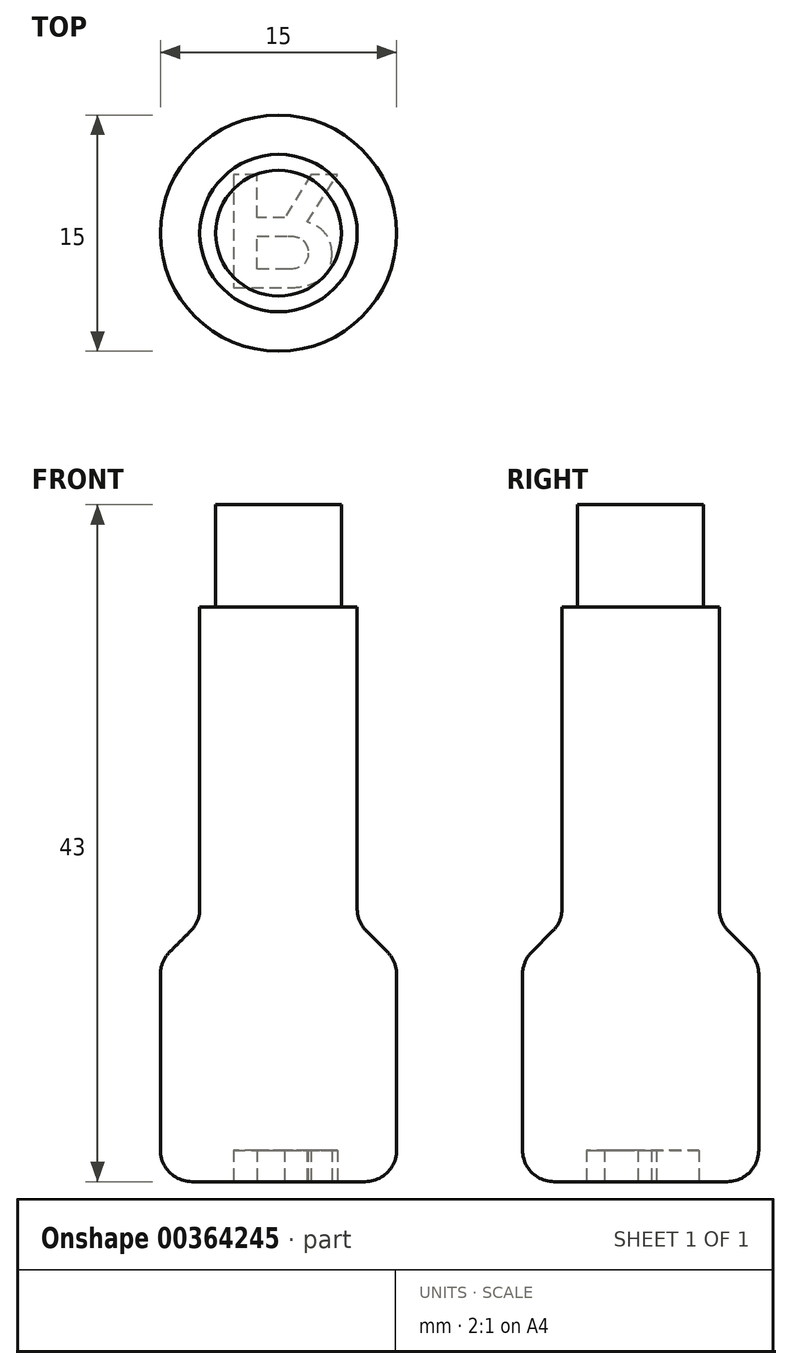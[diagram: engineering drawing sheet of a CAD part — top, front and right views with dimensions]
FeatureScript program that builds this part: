
annotation { "Feature Type Name" : "Feature", "Feature Type Description" : "" }
export const myFeature = defineFeature(function(context is Context, id is Id, definition is map)
    precondition{}
    {
        {
            var Q0;
            Q0=qCreatedBy(makeId("Right.planeOp"),FACE);
            var sketch = newSketch(context, id + "F0", { "sketchPlane" : qUnion([Q0])});
            skLineSegment(sketch, "E0", {"start": v(0, 0) * mm, "end": v(-7.5, 0) * mm});
            skLineSegment(sketch, "E1", {"start": v(-7.5, 0) * mm, "end": v(-7.5, 14) * mm});
            skLineSegment(sketch, "E2", {"start": v(-7.5, 14) * mm, "end": v(-5, 16.5) * mm});
            skLineSegment(sketch, "E3", {"start": v(-5, 16.5) * mm, "end": v(-5, 36.5) * mm});
            skLineSegment(sketch, "E4", {"start": v(-5, 36.5) * mm, "end": v(-4, 36.5) * mm});
            skLineSegment(sketch, "E5", {"start": v(-4, 36.5) * mm, "end": v(-4, 43) * mm});
            skLineSegment(sketch, "E6", {"start": v(-4, 43) * mm, "end": v(0, 43) * mm});
            skLineSegment(sketch, "E7", {"start": v(0, 43) * mm, "end": v(0, 0) * mm});
            skSolve(sketch);
        }
        {
            var Q0;
            Q0=makeQuery(id+"F0.imprint","IMPRINT",FACE,{"disambiguationData":[TD([[makeQuery(id+"F0.imprint","IMPRINT",EDGE,{"derivedFrom":sQuery(id+"F0.wireOp",EDGE,"E0")}),-1.0]])]});
            var Q1;
            Q1=sQuery(id+"F0.wireOp",EDGE,"E7");
            revolve(context, id + "F1", {"entities" : qUnion([Q0]), "axis" : qUnion([Q1]), "revolveType" : RevolveType.FULL});
        }
        {
            var Q0;
            Q0=makeQuery(id+"F1.opRevolve","SWEPT_EDGE",EDGE,{"disambiguationData":[OSD([sQuery(id+"F0.wireOp",EDGE,"E0"),sQuery(id+"F0.wireOp",EDGE,"E1")])]});
            var Q1;
            Q1=makeQuery(id+"F1.opRevolve","SWEPT_EDGE",EDGE,{"disambiguationData":[OSD([sQuery(id+"F0.wireOp",EDGE,"E1"),sQuery(id+"F0.wireOp",EDGE,"E2")])]});
            var Q2;
            Q2=makeQuery(id+"F1.opRevolve","SWEPT_EDGE",EDGE,{"disambiguationData":[OSD([sQuery(id+"F0.wireOp",EDGE,"E2"),sQuery(id+"F0.wireOp",EDGE,"E3")])]});
            fillet(context, id + "F2", {"entities" : qUnion([Q0, Q1, Q2]), "radius" : 2 * mm, "tangentPropagation" : true, "allowEdgeOverflow" : false});
        }
        {
            var Q0;
            Q0=makeQuery(id+"F1.opRevolve","SWEPT_FACE",FACE,{"disambiguationData":[OSD([sQuery(id+"F0.wireOp",EDGE,"E0")])]});
            var sketch = newSketch(context, id + "F3", { "sketchPlane" : qUnion([Q0])});
            skText(sketch, "E8", { "text": "R", "fontName": "Arimo-Bold.ttf"});
            const initialGuessF3  = {"E8": [-0.00356, -0.00371, 1, 0, 0.0075]};
            skSetInitialGuess(sketch, initialGuessF3);
            skSolve(sketch);
        }
        {
            var Q0;
            Q0=makeQuery(id+"F3.imprint","IMPRINT",FACE,{"disambiguationData":[TD([[makeQuery(id+"F3.imprint","IMPRINT",EDGE,{"derivedFrom":sQuery(id+"F3.wireOp",EDGE,"E8.sketch_text.stroke-0")}),-1.0]])]});
            extrude(context, id + "F4", {"entities" : qUnion([Q0]), "operationType" : NewBodyOperationType.REMOVE, "oppositeDirection" : true, "depth" : 2 * mm});
        }
    });
